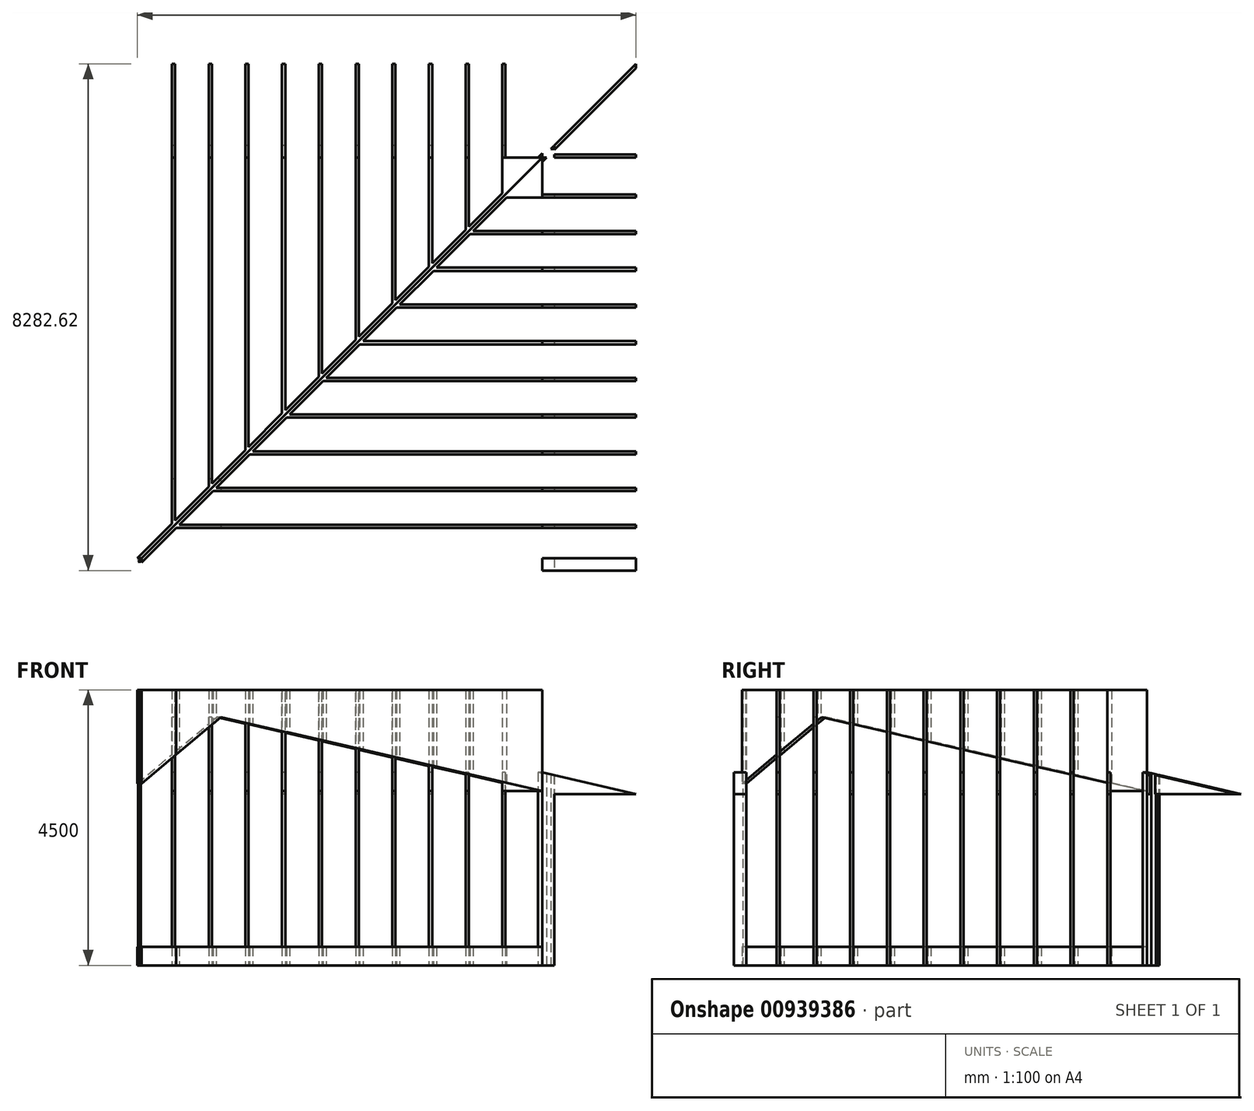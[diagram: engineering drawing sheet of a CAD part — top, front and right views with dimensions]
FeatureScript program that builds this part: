
annotation { "Feature Type Name" : "Feature", "Feature Type Description" : "" }
export const myFeature = defineFeature(function(context is Context, id is Id, definition is map)
    precondition{}
    {
        {
            var Q0;
            Q0=qCreatedBy(makeId("Top.planeOp"),FACE);
            var sketch = newSketch(context, id + "F0", { "sketchPlane" : qUnion([Q0])});
            skLineSegment(sketch, "E0.bottom", {"start": v(0, 0) * mm, "end": v(-6549, 0) * mm});
            skLineSegment(sketch, "E0.top", {"start": v(0, -6549) * mm, "end": v(-6549, -6549) * mm});
            skLineSegment(sketch, "E0.left", {"start": v(0, 0) * mm, "end": v(0, -6549) * mm});
            skLineSegment(sketch, "E0.right", {"start": v(-6549, 0) * mm, "end": v(-6549, -6549) * mm});
            skLineSegment(sketch, "E1.bottom", {"start": v(200, 200) * mm, "end": v(-6749, 200) * mm});
            skLineSegment(sketch, "E1.top", {"start": v(200, -6749) * mm, "end": v(-6749, -6749) * mm});
            skLineSegment(sketch, "E1.left", {"start": v(200, 200) * mm, "end": v(200, -6749) * mm});
            skLineSegment(sketch, "E1.right", {"start": v(-6749, 200) * mm, "end": v(-6749, -6749) * mm});
            skLineSegment(sketch, "E2.bottom", {"start": v(200, 200) * mm, "end": v(0, 200) * mm});
            skLineSegment(sketch, "E2.top", {"start": v(200, 0) * mm, "end": v(0, 0) * mm});
            skLineSegment(sketch, "E2.left", {"start": v(200, 200) * mm, "end": v(200, 0) * mm});
            skLineSegment(sketch, "E2.right", {"start": v(0, 200) * mm, "end": v(0, 0) * mm});
            skLineSegment(sketch, "E3.bottom", {"start": v(-6749, -6749) * mm, "end": v(-6549, -6749) * mm});
            skLineSegment(sketch, "E3.top", {"start": v(-6749, -6549) * mm, "end": v(-6549, -6549) * mm});
            skLineSegment(sketch, "E3.left", {"start": v(-6749, -6749) * mm, "end": v(-6749, -6549) * mm});
            skLineSegment(sketch, "E3.right", {"start": v(-6549, -6749) * mm, "end": v(-6549, -6549) * mm});
            skLineSegment(sketch, "E4", {"start": v(-6749, -6679) * mm, "end": v(130, 200) * mm});
            skLineSegment(sketch, "E5", {"start": v(200, 130) * mm, "end": v(-6679, -6749) * mm});
            skLineSegment(sketch, "E6", {"start": v(0, -600) * mm, "end": v(-530, -600) * mm});
            skLineSegment(sketch, "E7", {"start": v(0, -651) * mm, "end": v(-581, -651) * mm});
            skLineSegment(sketch, "E8", {"start": v(0, -1200) * mm, "end": v(-1130, -1200) * mm});
            skLineSegment(sketch, "E9", {"start": v(0, -1251) * mm, "end": v(-1181, -1251) * mm});
            skLineSegment(sketch, "E10", {"start": v(0, -1800) * mm, "end": v(-1730, -1800) * mm});
            skLineSegment(sketch, "E11", {"start": v(0, -1851) * mm, "end": v(-1781, -1851) * mm});
            skLineSegment(sketch, "E12", {"start": v(0, -2400) * mm, "end": v(-2330, -2400) * mm});
            skLineSegment(sketch, "E13", {"start": v(-2381, -2451) * mm, "end": v(0, -2451) * mm});
            skLineSegment(sketch, "E14", {"start": v(-2930, -3000) * mm, "end": v(0, -3000) * mm});
            skLineSegment(sketch, "E15", {"start": v(-3530, -3600) * mm, "end": v(0, -3600) * mm});
            skLineSegment(sketch, "E16", {"start": v(-2981, -3051) * mm, "end": v(0, -3051) * mm});
            skLineSegment(sketch, "E17", {"start": v(-3581, -3651) * mm, "end": v(0, -3651) * mm});
            skLineSegment(sketch, "E18", {"start": v(-4130, -4200) * mm, "end": v(0, -4200) * mm});
            skLineSegment(sketch, "E19", {"start": v(-4181, -4251) * mm, "end": v(0, -4251) * mm});
            skLineSegment(sketch, "E20", {"start": v(-4730, -4800) * mm, "end": v(0, -4800) * mm});
            skLineSegment(sketch, "E21", {"start": v(-4781, -4851) * mm, "end": v(0, -4851) * mm});
            skLineSegment(sketch, "E22", {"start": v(-5330, -5400) * mm, "end": v(0, -5400) * mm});
            skLineSegment(sketch, "E23", {"start": v(0, -5451) * mm, "end": v(-5381, -5451) * mm});
            skLineSegment(sketch, "E24", {"start": v(-5930, -6000) * mm, "end": v(0, -6000) * mm});
            skLineSegment(sketch, "E25", {"start": v(0, -6051) * mm, "end": v(-5981, -6051) * mm});
            skLineSegment(sketch, "E26", {"start": v(-6749, -6749) * mm, "end": v(200, 200) * mm});
            skLineSegment(sketch, "E27.bottom", {"start": v(0, -6000) * mm, "end": v(200, -6000) * mm});
            skLineSegment(sketch, "E27.top", {"start": v(0, -6051) * mm, "end": v(200, -6051) * mm});
            skLineSegment(sketch, "E27.left", {"start": v(0, -6000) * mm, "end": v(0, -6051) * mm});
            skLineSegment(sketch, "E27.right", {"start": v(200, -6000) * mm, "end": v(200, -6051) * mm});
            skLineSegment(sketch, "E28.bottom", {"start": v(0, -6549) * mm, "end": v(200, -6549) * mm});
            skLineSegment(sketch, "E28.top", {"start": v(0, -6749) * mm, "end": v(200, -6749) * mm});
            skLineSegment(sketch, "E28.left", {"start": v(0, -6549) * mm, "end": v(0, -6749) * mm});
            skLineSegment(sketch, "E28.right", {"start": v(200, -6549) * mm, "end": v(200, -6749) * mm});
            skLineSegment(sketch, "E29.bottom", {"start": v(0, -5400) * mm, "end": v(200, -5400) * mm});
            skLineSegment(sketch, "E29.top", {"start": v(0, -5451) * mm, "end": v(200, -5451) * mm});
            skLineSegment(sketch, "E29.left", {"start": v(0, -5400) * mm, "end": v(0, -5451) * mm});
            skLineSegment(sketch, "E29.right", {"start": v(200, -5400) * mm, "end": v(200, -5451) * mm});
            skLineSegment(sketch, "E30.bottom", {"start": v(0, -4800) * mm, "end": v(200, -4800) * mm});
            skLineSegment(sketch, "E30.top", {"start": v(0, -4851) * mm, "end": v(200, -4851) * mm});
            skLineSegment(sketch, "E30.left", {"start": v(0, -4800) * mm, "end": v(0, -4851) * mm});
            skLineSegment(sketch, "E30.right", {"start": v(200, -4800) * mm, "end": v(200, -4851) * mm});
            skLineSegment(sketch, "E31.bottom", {"start": v(0, -4200) * mm, "end": v(200, -4200) * mm});
            skLineSegment(sketch, "E31.top", {"start": v(0, -4251) * mm, "end": v(200, -4251) * mm});
            skLineSegment(sketch, "E31.left", {"start": v(0, -4200) * mm, "end": v(0, -4251) * mm});
            skLineSegment(sketch, "E31.right", {"start": v(200, -4200) * mm, "end": v(200, -4251) * mm});
            skLineSegment(sketch, "E32.bottom", {"start": v(0, -3600) * mm, "end": v(200, -3600) * mm});
            skLineSegment(sketch, "E32.top", {"start": v(0, -3651) * mm, "end": v(200, -3651) * mm});
            skLineSegment(sketch, "E32.left", {"start": v(0, -3600) * mm, "end": v(0, -3651) * mm});
            skLineSegment(sketch, "E32.right", {"start": v(200, -3600) * mm, "end": v(200, -3651) * mm});
            skLineSegment(sketch, "E33.bottom", {"start": v(0, -3000) * mm, "end": v(200, -3000) * mm});
            skLineSegment(sketch, "E33.top", {"start": v(0, -3051) * mm, "end": v(200, -3051) * mm});
            skLineSegment(sketch, "E33.left", {"start": v(0, -3000) * mm, "end": v(0, -3051) * mm});
            skLineSegment(sketch, "E33.right", {"start": v(200, -3000) * mm, "end": v(200, -3051) * mm});
            skLineSegment(sketch, "E34.bottom", {"start": v(0, -2400) * mm, "end": v(200, -2400) * mm});
            skLineSegment(sketch, "E34.top", {"start": v(0, -2451) * mm, "end": v(200, -2451) * mm});
            skLineSegment(sketch, "E34.left", {"start": v(0, -2400) * mm, "end": v(0, -2451) * mm});
            skLineSegment(sketch, "E34.right", {"start": v(200, -2400) * mm, "end": v(200, -2451) * mm});
            skLineSegment(sketch, "E35.bottom", {"start": v(0, -1800) * mm, "end": v(200, -1800) * mm});
            skLineSegment(sketch, "E35.top", {"start": v(0, -1851) * mm, "end": v(200, -1851) * mm});
            skLineSegment(sketch, "E35.left", {"start": v(0, -1800) * mm, "end": v(0, -1851) * mm});
            skLineSegment(sketch, "E35.right", {"start": v(200, -1800) * mm, "end": v(200, -1851) * mm});
            skLineSegment(sketch, "E36.bottom", {"start": v(0, -1200) * mm, "end": v(200, -1200) * mm});
            skLineSegment(sketch, "E36.top", {"start": v(0, -1251) * mm, "end": v(200, -1251) * mm});
            skLineSegment(sketch, "E36.left", {"start": v(0, -1200) * mm, "end": v(0, -1251) * mm});
            skLineSegment(sketch, "E36.right", {"start": v(200, -1200) * mm, "end": v(200, -1251) * mm});
            skLineSegment(sketch, "E37.bottom", {"start": v(0, -600) * mm, "end": v(200, -600) * mm});
            skLineSegment(sketch, "E37.top", {"start": v(0, -651) * mm, "end": v(200, -651) * mm});
            skLineSegment(sketch, "E37.left", {"start": v(0, -600) * mm, "end": v(0, -651) * mm});
            skLineSegment(sketch, "E37.right", {"start": v(200, -600) * mm, "end": v(200, -651) * mm});
            skLineSegment(sketch, "E38.bottom", {"start": v(188, 12) * mm, "end": v(12, 12) * mm});
            skLineSegment(sketch, "E38.top", {"start": v(188, 188) * mm, "end": v(12, 188) * mm});
            skLineSegment(sketch, "E38.left", {"start": v(188, 12) * mm, "end": v(188, 188) * mm});
            skLineSegment(sketch, "E38.right", {"start": v(12, 12) * mm, "end": v(12, 188) * mm});
            skLineSegment(sketch, "E39.bottom", {"start": v(188, 12) * mm, "end": v(143, 12) * mm});
            skLineSegment(sketch, "E39.top", {"start": v(188, 57) * mm, "end": v(143, 57) * mm});
            skLineSegment(sketch, "E39.left", {"start": v(188, 12) * mm, "end": v(188, 57) * mm});
            skLineSegment(sketch, "E39.right", {"start": v(143, 12) * mm, "end": v(143, 57) * mm});
            skLineSegment(sketch, "E40.bottom", {"start": v(12, 12) * mm, "end": v(57, 12) * mm});
            skLineSegment(sketch, "E40.top", {"start": v(12, 57) * mm, "end": v(57, 57) * mm});
            skLineSegment(sketch, "E40.left", {"start": v(12, 12) * mm, "end": v(12, 57) * mm});
            skLineSegment(sketch, "E40.right", {"start": v(57, 12) * mm, "end": v(57, 57) * mm});
            skLineSegment(sketch, "E41.bottom", {"start": v(188, 188) * mm, "end": v(143, 188) * mm});
            skLineSegment(sketch, "E41.top", {"start": v(188, 143) * mm, "end": v(143, 143) * mm});
            skLineSegment(sketch, "E41.left", {"start": v(188, 188) * mm, "end": v(188, 143) * mm});
            skLineSegment(sketch, "E41.right", {"start": v(143, 188) * mm, "end": v(143, 143) * mm});
            skLineSegment(sketch, "E42.bottom", {"start": v(12, 188) * mm, "end": v(57, 188) * mm});
            skLineSegment(sketch, "E42.top", {"start": v(12, 143) * mm, "end": v(57, 143) * mm});
            skLineSegment(sketch, "E42.left", {"start": v(12, 188) * mm, "end": v(12, 143) * mm});
            skLineSegment(sketch, "E42.right", {"start": v(57, 188) * mm, "end": v(57, 143) * mm});
            skLineSegment(sketch, "E43.bottom", {"start": v(200, -6749) * mm, "end": v(1700, -6749) * mm});
            skLineSegment(sketch, "E43.top", {"start": v(200, 200) * mm, "end": v(1700, 200) * mm});
            skLineSegment(sketch, "E43.left", {"start": v(200, -6749) * mm, "end": v(200, 200) * mm});
            skLineSegment(sketch, "E43.right", {"start": v(1700, -6749) * mm, "end": v(1700, 200) * mm});
            skLineSegment(sketch, "E44.bottom", {"start": v(200, -6549) * mm, "end": v(1700, -6549) * mm});
            skLineSegment(sketch, "E44.right", {"start": v(1700, -6549) * mm, "end": v(1700, -6749) * mm});
            skLineSegment(sketch, "E45.bottom", {"start": v(200, -6000) * mm, "end": v(1700, -6000) * mm});
            skLineSegment(sketch, "E45.top", {"start": v(200, -6051) * mm, "end": v(1700, -6051) * mm});
            skLineSegment(sketch, "E45.right", {"start": v(1700, -6000) * mm, "end": v(1700, -6051) * mm});
            skLineSegment(sketch, "E46.bottom", {"start": v(200, -5400) * mm, "end": v(1700, -5400) * mm});
            skLineSegment(sketch, "E46.top", {"start": v(200, -5451) * mm, "end": v(1700, -5451) * mm});
            skLineSegment(sketch, "E46.right", {"start": v(1700, -5400) * mm, "end": v(1700, -5451) * mm});
            skLineSegment(sketch, "E47.bottom", {"start": v(200, -4800) * mm, "end": v(1700, -4800) * mm});
            skLineSegment(sketch, "E47.top", {"start": v(200, -4851) * mm, "end": v(1700, -4851) * mm});
            skLineSegment(sketch, "E47.right", {"start": v(1700, -4800) * mm, "end": v(1700, -4851) * mm});
            skLineSegment(sketch, "E48.bottom", {"start": v(200, -4200) * mm, "end": v(1700, -4200) * mm});
            skLineSegment(sketch, "E48.top", {"start": v(200, -4251) * mm, "end": v(1700, -4251) * mm});
            skLineSegment(sketch, "E48.right", {"start": v(1700, -4200) * mm, "end": v(1700, -4251) * mm});
            skLineSegment(sketch, "E49.bottom", {"start": v(200, -3600) * mm, "end": v(1700, -3600) * mm});
            skLineSegment(sketch, "E49.top", {"start": v(200, -3651) * mm, "end": v(1700, -3651) * mm});
            skLineSegment(sketch, "E49.right", {"start": v(1700, -3600) * mm, "end": v(1700, -3651) * mm});
            skLineSegment(sketch, "E50.bottom", {"start": v(200, -3000) * mm, "end": v(1700, -3000) * mm});
            skLineSegment(sketch, "E50.top", {"start": v(200, -3051) * mm, "end": v(1700, -3051) * mm});
            skLineSegment(sketch, "E50.right", {"start": v(1700, -3000) * mm, "end": v(1700, -3051) * mm});
            skLineSegment(sketch, "E51.bottom", {"start": v(200, -2400) * mm, "end": v(1700, -2400) * mm});
            skLineSegment(sketch, "E51.top", {"start": v(200, -2451) * mm, "end": v(1700, -2451) * mm});
            skLineSegment(sketch, "E51.right", {"start": v(1700, -2400) * mm, "end": v(1700, -2451) * mm});
            skLineSegment(sketch, "E52.bottom", {"start": v(200, -1800) * mm, "end": v(1700, -1800) * mm});
            skLineSegment(sketch, "E52.top", {"start": v(200, -1851) * mm, "end": v(1700, -1851) * mm});
            skLineSegment(sketch, "E52.right", {"start": v(1700, -1800) * mm, "end": v(1700, -1851) * mm});
            skLineSegment(sketch, "E53.bottom", {"start": v(200, -1200) * mm, "end": v(1700, -1200) * mm});
            skLineSegment(sketch, "E53.top", {"start": v(200, -1251) * mm, "end": v(1700, -1251) * mm});
            skLineSegment(sketch, "E53.right", {"start": v(1700, -1200) * mm, "end": v(1700, -1251) * mm});
            skLineSegment(sketch, "E54.bottom", {"start": v(200, -600) * mm, "end": v(1700, -600) * mm});
            skLineSegment(sketch, "E54.top", {"start": v(200, -651) * mm, "end": v(1700, -651) * mm});
            skLineSegment(sketch, "E54.right", {"start": v(1700, -600) * mm, "end": v(1700, -651) * mm});
            skLineSegment(sketch, "E55.bottom", {"start": v(200, 0) * mm, "end": v(1700, 0) * mm});
            skLineSegment(sketch, "E55.top", {"start": v(200, 51) * mm, "end": v(1700, 51) * mm});
            skLineSegment(sketch, "E55.left", {"start": v(200, 0) * mm, "end": v(200, 51) * mm});
            skLineSegment(sketch, "E55.right", {"start": v(1700, 0) * mm, "end": v(1700, 51) * mm});
            skLineSegment(sketch, "E56.bottom", {"start": v(-6737, -6561) * mm, "end": v(-6561, -6561) * mm});
            skLineSegment(sketch, "E56.top", {"start": v(-6737, -6737) * mm, "end": v(-6561, -6737) * mm});
            skLineSegment(sketch, "E56.left", {"start": v(-6737, -6561) * mm, "end": v(-6737, -6737) * mm});
            skLineSegment(sketch, "E56.right", {"start": v(-6561, -6561) * mm, "end": v(-6561, -6737) * mm});
            skLineSegment(sketch, "E57.bottom", {"start": v(-6737, -6561) * mm, "end": v(-6692, -6561) * mm});
            skLineSegment(sketch, "E57.top", {"start": v(-6737, -6606) * mm, "end": v(-6692, -6606) * mm});
            skLineSegment(sketch, "E57.left", {"start": v(-6737, -6561) * mm, "end": v(-6737, -6606) * mm});
            skLineSegment(sketch, "E57.right", {"start": v(-6692, -6561) * mm, "end": v(-6692, -6606) * mm});
            skLineSegment(sketch, "E58.bottom", {"start": v(-6737, -6737) * mm, "end": v(-6692, -6737) * mm});
            skLineSegment(sketch, "E58.top", {"start": v(-6737, -6692) * mm, "end": v(-6692, -6692) * mm});
            skLineSegment(sketch, "E58.left", {"start": v(-6737, -6737) * mm, "end": v(-6737, -6692) * mm});
            skLineSegment(sketch, "E58.right", {"start": v(-6692, -6737) * mm, "end": v(-6692, -6692) * mm});
            skLineSegment(sketch, "E59.bottom", {"start": v(-6561, -6561) * mm, "end": v(-6606, -6561) * mm});
            skLineSegment(sketch, "E59.top", {"start": v(-6561, -6606) * mm, "end": v(-6606, -6606) * mm});
            skLineSegment(sketch, "E59.left", {"start": v(-6561, -6561) * mm, "end": v(-6561, -6606) * mm});
            skLineSegment(sketch, "E59.right", {"start": v(-6606, -6561) * mm, "end": v(-6606, -6606) * mm});
            skLineSegment(sketch, "E60.bottom", {"start": v(-6561, -6737) * mm, "end": v(-6606, -6737) * mm});
            skLineSegment(sketch, "E60.top", {"start": v(-6561, -6692) * mm, "end": v(-6606, -6692) * mm});
            skLineSegment(sketch, "E60.left", {"start": v(-6561, -6737) * mm, "end": v(-6561, -6692) * mm});
            skLineSegment(sketch, "E60.right", {"start": v(-6606, -6737) * mm, "end": v(-6606, -6692) * mm});
            skLineSegment(sketch, "E61", {"start": v(200, 130) * mm, "end": v(1700, 1630) * mm});
            skLineSegment(sketch, "E62", {"start": v(130, 200) * mm, "end": v(1700, 1770) * mm});
            skPoint(sketch, "E62.endSnap0", {"position": v(1700, 25.5) * mm});
            skLineSegment(sketch, "E63", {"start": v(1700, 1770) * mm, "end": v(1700, 1630) * mm});
            skLineSegment(sketch, "E64", {"start": v(200, 200) * mm, "end": v(1700, 1700) * mm});
            skSolve(sketch);
        }
        {
            var Q0;
            {var subQ1=sQuery(id+"F0.wireOp",EDGE,"E3.bottom");var subQ3=sQuery(id+"F0.wireOp",EDGE,"E5");var subQ4=makeQuery(id+"F0.imprint","INTERSECT",VERTEX,{"derivedFrom":[subQ1,subQ3]});Q0=makeQuery(id+"F0.imprint","IMPRINT",FACE,{"disambiguationData":[TD([[makeQuery(id+"F0.imprint","IMPRINT",EDGE,{"disambiguationData":[TD([[subQ4,1.0]])],"derivedFrom":subQ3}),1.0]])]});}
            var Q1;
            {var subQ3=sQuery(id+"F0.wireOp",EDGE,"E5");var subQ5=sQuery(id+"F0.wireOp",EDGE,"E2.left");var subQ7=makeQuery(id+"F0.imprint","INTERSECT",VERTEX,{"derivedFrom":[subQ5,subQ3]});Q1=makeQuery(id+"F0.imprint","IMPRINT",FACE,{"disambiguationData":[TD([[makeQuery(id+"F0.imprint","IMPRINT",EDGE,{"disambiguationData":[TD([[subQ7,-1.0]])],"derivedFrom":subQ3}),-1.0]])]});}
            var Q2;
            {var subQ1=sQuery(id+"F0.wireOp",EDGE,"E3.bottom");var subQ3=sQuery(id+"F0.wireOp",EDGE,"E5");var subQ4=makeQuery(id+"F0.imprint","INTERSECT",VERTEX,{"derivedFrom":[subQ1,subQ3]});Q2=makeQuery(id+"F0.imprint","IMPRINT",FACE,{"disambiguationData":[TD([[makeQuery(id+"F0.imprint","IMPRINT",EDGE,{"disambiguationData":[TD([[subQ4,1.0]])],"derivedFrom":subQ3}),-1.0]])]});}
            var Q3;
            {var subQ28=sQuery(id+"F0.wireOp",EDGE,"E1.top");Q3=makeQuery(id+"F0.imprint","IMPRINT",FACE,{"disambiguationData":[TD([[makeQuery(id+"F0.imprint","IMPRINT",EDGE,{"derivedFrom":subQ28}),-1.0]])]});}
            var Q4;
            {var subQ1=sQuery(id+"F0.wireOp",EDGE,"E0.top");var subQ3=sQuery(id+"F0.wireOp",EDGE,"E5");var subQ4=makeQuery(id+"F0.imprint","INTERSECT",VERTEX,{"derivedFrom":[subQ1,subQ3]});Q4=makeQuery(id+"F0.imprint","IMPRINT",FACE,{"disambiguationData":[TD([[makeQuery(id+"F0.imprint","IMPRINT",EDGE,{"disambiguationData":[TD([[subQ4,-1.0]])],"derivedFrom":subQ3}),-1.0]])]});}
            var Q5;
            {var subQ0=sQuery(id+"F0.wireOp",EDGE,"E5");var subQ13=makeQuery(id+"F0.imprint","INTERSECT",VERTEX,{"derivedFrom":[subQ0,sQuery(id+"F0.wireOp",EDGE,"E6")]});Q5=makeQuery(id+"F0.imprint","IMPRINT",FACE,{"disambiguationData":[TD([[makeQuery(id+"F0.imprint","IMPRINT",EDGE,{"disambiguationData":[TD([[subQ13,1.0]])],"derivedFrom":subQ0}),-1.0]])]});}
            var Q6;
            {var subQ0=sQuery(id+"F0.wireOp",EDGE,"E24");Q6=makeQuery(id+"F0.imprint","IMPRINT",FACE,{"disambiguationData":[TD([[makeQuery(id+"F0.imprint","IMPRINT",EDGE,{"derivedFrom":subQ0}),-1.0]])]});}
            var Q7;
            {var subQ0=sQuery(id+"F0.wireOp",EDGE,"E22");Q7=makeQuery(id+"F0.imprint","IMPRINT",FACE,{"disambiguationData":[TD([[makeQuery(id+"F0.imprint","IMPRINT",EDGE,{"derivedFrom":subQ0}),-1.0]])]});}
            var Q8;
            {var subQ0=sQuery(id+"F0.wireOp",EDGE,"E20");Q8=makeQuery(id+"F0.imprint","IMPRINT",FACE,{"disambiguationData":[TD([[makeQuery(id+"F0.imprint","IMPRINT",EDGE,{"derivedFrom":subQ0}),-1.0]])]});}
            var Q9;
            {var subQ0=sQuery(id+"F0.wireOp",EDGE,"E18");Q9=makeQuery(id+"F0.imprint","IMPRINT",FACE,{"disambiguationData":[TD([[makeQuery(id+"F0.imprint","IMPRINT",EDGE,{"derivedFrom":subQ0}),-1.0]])]});}
            var Q10;
            {var subQ0=sQuery(id+"F0.wireOp",EDGE,"E15");Q10=makeQuery(id+"F0.imprint","IMPRINT",FACE,{"disambiguationData":[TD([[makeQuery(id+"F0.imprint","IMPRINT",EDGE,{"derivedFrom":subQ0}),-1.0]])]});}
            var Q11;
            {var subQ0=sQuery(id+"F0.wireOp",EDGE,"E14");Q11=makeQuery(id+"F0.imprint","IMPRINT",FACE,{"disambiguationData":[TD([[makeQuery(id+"F0.imprint","IMPRINT",EDGE,{"derivedFrom":subQ0}),-1.0]])]});}
            var Q12;
            {var subQ0=sQuery(id+"F0.wireOp",EDGE,"E12");Q12=makeQuery(id+"F0.imprint","IMPRINT",FACE,{"disambiguationData":[TD([[makeQuery(id+"F0.imprint","IMPRINT",EDGE,{"derivedFrom":subQ0}),1.0]])]});}
            var Q13;
            {var subQ0=sQuery(id+"F0.wireOp",EDGE,"E10");Q13=makeQuery(id+"F0.imprint","IMPRINT",FACE,{"disambiguationData":[TD([[makeQuery(id+"F0.imprint","IMPRINT",EDGE,{"derivedFrom":subQ0}),1.0]])]});}
            var Q14;
            {var subQ0=sQuery(id+"F0.wireOp",EDGE,"E8");Q14=makeQuery(id+"F0.imprint","IMPRINT",FACE,{"disambiguationData":[TD([[makeQuery(id+"F0.imprint","IMPRINT",EDGE,{"derivedFrom":subQ0}),1.0]])]});}
            var Q15;
            {var subQ0=sQuery(id+"F0.wireOp",EDGE,"E6");Q15=makeQuery(id+"F0.imprint","IMPRINT",FACE,{"disambiguationData":[TD([[makeQuery(id+"F0.imprint","IMPRINT",EDGE,{"derivedFrom":subQ0}),1.0]])]});}
            var Q16;
            {var subQ1=sQuery(id+"F0.wireOp",EDGE,"E0.left");var subQ3=sQuery(id+"F0.wireOp",EDGE,"E5");var subQ4=makeQuery(id+"F0.imprint","INTERSECT",VERTEX,{"derivedFrom":[subQ1,subQ3]});Q16=makeQuery(id+"F0.imprint","IMPRINT",FACE,{"disambiguationData":[TD([[makeQuery(id+"F0.imprint","IMPRINT",EDGE,{"disambiguationData":[TD([[subQ4,1.0]])],"derivedFrom":subQ3}),-1.0]])]});}
            var Q17;
            Q17=makeQuery(id+"F0.imprint","IMPRINT",FACE,{"disambiguationData":[TD([[makeQuery(id+"F0.imprint","IMPRINT",EDGE,{"derivedFrom":sQuery(id+"F0.wireOp",EDGE,"E28.bottom")}),-1.0]])]});
            var Q18;
            Q18=makeQuery(id+"F0.imprint","IMPRINT",FACE,{"disambiguationData":[TD([[makeQuery(id+"F0.imprint","IMPRINT",EDGE,{"derivedFrom":sQuery(id+"F0.wireOp",EDGE,"E27.bottom")}),-1.0]])]});
            var Q19;
            Q19=makeQuery(id+"F0.imprint","IMPRINT",FACE,{"disambiguationData":[TD([[makeQuery(id+"F0.imprint","IMPRINT",EDGE,{"derivedFrom":sQuery(id+"F0.wireOp",EDGE,"E29.bottom")}),-1.0]])]});
            var Q20;
            Q20=makeQuery(id+"F0.imprint","IMPRINT",FACE,{"disambiguationData":[TD([[makeQuery(id+"F0.imprint","IMPRINT",EDGE,{"derivedFrom":sQuery(id+"F0.wireOp",EDGE,"E30.bottom")}),-1.0]])]});
            var Q21;
            Q21=makeQuery(id+"F0.imprint","IMPRINT",FACE,{"disambiguationData":[TD([[makeQuery(id+"F0.imprint","IMPRINT",EDGE,{"derivedFrom":sQuery(id+"F0.wireOp",EDGE,"E31.bottom")}),-1.0]])]});
            var Q22;
            Q22=makeQuery(id+"F0.imprint","IMPRINT",FACE,{"disambiguationData":[TD([[makeQuery(id+"F0.imprint","IMPRINT",EDGE,{"derivedFrom":sQuery(id+"F0.wireOp",EDGE,"E32.bottom")}),-1.0]])]});
            var Q23;
            Q23=makeQuery(id+"F0.imprint","IMPRINT",FACE,{"disambiguationData":[TD([[makeQuery(id+"F0.imprint","IMPRINT",EDGE,{"derivedFrom":sQuery(id+"F0.wireOp",EDGE,"E33.bottom")}),-1.0]])]});
            var Q24;
            Q24=makeQuery(id+"F0.imprint","IMPRINT",FACE,{"disambiguationData":[TD([[makeQuery(id+"F0.imprint","IMPRINT",EDGE,{"derivedFrom":sQuery(id+"F0.wireOp",EDGE,"E34.bottom")}),-1.0]])]});
            var Q25;
            Q25=makeQuery(id+"F0.imprint","IMPRINT",FACE,{"disambiguationData":[TD([[makeQuery(id+"F0.imprint","IMPRINT",EDGE,{"derivedFrom":sQuery(id+"F0.wireOp",EDGE,"E35.bottom")}),-1.0]])]});
            var Q26;
            Q26=makeQuery(id+"F0.imprint","IMPRINT",FACE,{"disambiguationData":[TD([[makeQuery(id+"F0.imprint","IMPRINT",EDGE,{"derivedFrom":sQuery(id+"F0.wireOp",EDGE,"E36.bottom")}),-1.0]])]});
            var Q27;
            Q27=makeQuery(id+"F0.imprint","IMPRINT",FACE,{"disambiguationData":[TD([[makeQuery(id+"F0.imprint","IMPRINT",EDGE,{"derivedFrom":sQuery(id+"F0.wireOp",EDGE,"E37.bottom")}),-1.0]])]});
            var Q28;
            {var subQ0=sQuery(id+"F0.wireOp",EDGE,"E40.bottom");Q28=makeQuery(id+"F0.imprint","IMPRINT",FACE,{"disambiguationData":[TD([[makeQuery(id+"F0.imprint","IMPRINT",EDGE,{"derivedFrom":subQ0}),-1.0]])]});}
            var Q29;
            {var subQ0=sQuery(id+"F0.wireOp",EDGE,"E40.bottom");Q29=makeQuery(id+"F0.imprint","IMPRINT",FACE,{"disambiguationData":[TD([[makeQuery(id+"F0.imprint","IMPRINT",EDGE,{"derivedFrom":subQ0}),1.0]])]});}
            var Q30;
            Q30=makeQuery(id+"F0.imprint","IMPRINT",FACE,{"disambiguationData":[TD([[makeQuery(id+"F0.imprint","IMPRINT",EDGE,{"derivedFrom":sQuery(id+"F0.wireOp",EDGE,"E39.bottom")}),-1.0]])]});
            var Q31;
            {var subQ2=sQuery(id+"F0.wireOp",EDGE,"E41.top");Q31=makeQuery(id+"F0.imprint","IMPRINT",FACE,{"disambiguationData":[TD([[makeQuery(id+"F0.imprint","IMPRINT",EDGE,{"derivedFrom":subQ2}),-1.0]])]});}
            var Q32;
            Q32=makeQuery(id+"F0.imprint","IMPRINT",FACE,{"disambiguationData":[TD([[makeQuery(id+"F0.imprint","IMPRINT",EDGE,{"derivedFrom":sQuery(id+"F0.wireOp",EDGE,"E44.bottom")}),-1.0]])]});
            var Q33;
            Q33=makeQuery(id+"F0.imprint","IMPRINT",FACE,{"disambiguationData":[TD([[makeQuery(id+"F0.imprint","IMPRINT",EDGE,{"derivedFrom":sQuery(id+"F0.wireOp",EDGE,"E45.bottom")}),-1.0]])]});
            var Q34;
            Q34=makeQuery(id+"F0.imprint","IMPRINT",FACE,{"disambiguationData":[TD([[makeQuery(id+"F0.imprint","IMPRINT",EDGE,{"derivedFrom":sQuery(id+"F0.wireOp",EDGE,"E46.bottom")}),-1.0]])]});
            var Q35;
            Q35=makeQuery(id+"F0.imprint","IMPRINT",FACE,{"disambiguationData":[TD([[makeQuery(id+"F0.imprint","IMPRINT",EDGE,{"derivedFrom":sQuery(id+"F0.wireOp",EDGE,"E47.bottom")}),-1.0]])]});
            var Q36;
            Q36=makeQuery(id+"F0.imprint","IMPRINT",FACE,{"disambiguationData":[TD([[makeQuery(id+"F0.imprint","IMPRINT",EDGE,{"derivedFrom":sQuery(id+"F0.wireOp",EDGE,"E48.bottom")}),-1.0]])]});
            var Q37;
            Q37=makeQuery(id+"F0.imprint","IMPRINT",FACE,{"disambiguationData":[TD([[makeQuery(id+"F0.imprint","IMPRINT",EDGE,{"derivedFrom":sQuery(id+"F0.wireOp",EDGE,"E49.bottom")}),-1.0]])]});
            var Q38;
            Q38=makeQuery(id+"F0.imprint","IMPRINT",FACE,{"disambiguationData":[TD([[makeQuery(id+"F0.imprint","IMPRINT",EDGE,{"derivedFrom":sQuery(id+"F0.wireOp",EDGE,"E50.bottom")}),-1.0]])]});
            var Q39;
            Q39=makeQuery(id+"F0.imprint","IMPRINT",FACE,{"disambiguationData":[TD([[makeQuery(id+"F0.imprint","IMPRINT",EDGE,{"derivedFrom":sQuery(id+"F0.wireOp",EDGE,"E51.bottom")}),-1.0]])]});
            var Q40;
            Q40=makeQuery(id+"F0.imprint","IMPRINT",FACE,{"disambiguationData":[TD([[makeQuery(id+"F0.imprint","IMPRINT",EDGE,{"derivedFrom":sQuery(id+"F0.wireOp",EDGE,"E52.bottom")}),-1.0]])]});
            var Q41;
            Q41=makeQuery(id+"F0.imprint","IMPRINT",FACE,{"disambiguationData":[TD([[makeQuery(id+"F0.imprint","IMPRINT",EDGE,{"derivedFrom":sQuery(id+"F0.wireOp",EDGE,"E53.bottom")}),-1.0]])]});
            var Q42;
            Q42=makeQuery(id+"F0.imprint","IMPRINT",FACE,{"disambiguationData":[TD([[makeQuery(id+"F0.imprint","IMPRINT",EDGE,{"derivedFrom":sQuery(id+"F0.wireOp",EDGE,"E54.bottom")}),-1.0]])]});
            var Q43;
            Q43=makeQuery(id+"F0.imprint","IMPRINT",FACE,{"disambiguationData":[TD([[makeQuery(id+"F0.imprint","IMPRINT",EDGE,{"derivedFrom":sQuery(id+"F0.wireOp",EDGE,"E55.bottom")}),1.0]])]});
            var Q44;
            {var subQ1=sQuery(id+"F0.wireOp",EDGE,"E3.bottom");var subQ3=sQuery(id+"F0.wireOp",EDGE,"E5");var subQ4=makeQuery(id+"F0.imprint","INTERSECT",VERTEX,{"derivedFrom":[subQ1,subQ3]});Q44=makeQuery(id+"F0.imprint","IMPRINT",FACE,{"disambiguationData":[TD([[makeQuery(id+"F0.imprint","IMPRINT",EDGE,{"disambiguationData":[TD([[subQ4,1.0]])],"derivedFrom":subQ3}),1.0]])]});}
            var Q45;
            {var subQ0=sQuery(id+"F0.wireOp",EDGE,"E39.bottom");Q45=makeQuery(id+"F0.imprint","IMPRINT",FACE,{"disambiguationData":[TD([[makeQuery(id+"F0.imprint","IMPRINT",EDGE,{"derivedFrom":subQ0}),1.0]])]});}
            var Q46;
            {var subQ0=sQuery(id+"F0.wireOp",EDGE,"E41.left");Q46=makeQuery(id+"F0.imprint","IMPRINT",FACE,{"disambiguationData":[TD([[makeQuery(id+"F0.imprint","IMPRINT",EDGE,{"derivedFrom":subQ0}),1.0]])]});}
            var Q47;
            {var subQ0=sQuery(id+"F0.wireOp",EDGE,"E58.bottom");Q47=makeQuery(id+"F0.imprint","IMPRINT",FACE,{"disambiguationData":[TD([[makeQuery(id+"F0.imprint","IMPRINT",EDGE,{"derivedFrom":subQ0}),1.0]])]});}
            var Q48;
            Q48=makeQuery(id+"F0.imprint","IMPRINT",FACE,{"disambiguationData":[TD([[makeQuery(id+"F0.imprint","IMPRINT",EDGE,{"derivedFrom":sQuery(id+"F0.wireOp",EDGE,"E60.bottom")}),-1.0]])]});
            var Q49;
            {var subQ2=sQuery(id+"F0.wireOp",EDGE,"E59.top");Q49=makeQuery(id+"F0.imprint","IMPRINT",FACE,{"disambiguationData":[TD([[makeQuery(id+"F0.imprint","IMPRINT",EDGE,{"derivedFrom":subQ2}),-1.0]])]});}
            var Q50;
            {var subQ0=sQuery(id+"F0.wireOp",EDGE,"E59.left");Q50=makeQuery(id+"F0.imprint","IMPRINT",FACE,{"disambiguationData":[TD([[makeQuery(id+"F0.imprint","IMPRINT",EDGE,{"derivedFrom":subQ0}),1.0]])]});}
            var Q51;
            {var subQ0=sQuery(id+"F0.wireOp",EDGE,"E64");Q51=makeQuery(id+"F0.imprint","IMPRINT",FACE,{"disambiguationData":[TD([[makeQuery(id+"F0.imprint","IMPRINT",EDGE,{"derivedFrom":subQ0}),-1.0]])]});}
            var Q52;
            {var subQ1=sQuery(id+"F0.wireOp",EDGE,"E43.top");var subQ3=sQuery(id+"F0.wireOp",EDGE,"E61");var subQ4=makeQuery(id+"F0.imprint","INTERSECT",VERTEX,{"derivedFrom":[subQ1,subQ3]});Q52=makeQuery(id+"F0.imprint","IMPRINT",FACE,{"disambiguationData":[TD([[makeQuery(id+"F0.imprint","IMPRINT",EDGE,{"disambiguationData":[TD([[subQ4,1.0]])],"derivedFrom":subQ3}),1.0]])]});}
            extrude(context, id + "F1", {"entities" : qUnion([Q0, Q1, Q2, Q3, Q4, Q5, Q6, Q7, Q8, Q9, Q10, Q11, Q12, Q13, Q14, Q15, Q16, Q17, Q18, Q19, Q20, Q21, Q22, Q23, Q24, Q25, Q26, Q27, Q28, Q29, Q30, Q31, Q32, Q33, Q34, Q35, Q36, Q37, Q38, Q39, Q40, Q41, Q42, Q43, Q44, Q45, Q46, Q47, Q48, Q49, Q50, Q51, Q52]), "depth" : 4500 * mm, "offsetDistance" : 25 * mm});
        }
        {
            var Q0;
            Q0=makeQuery(id+"F1.opExtrude","SWEPT_FACE",FACE,{"disambiguationData":[OSD([sQuery(id+"F0.wireOp",EDGE,"E1.top"),sQuery(id+"F0.wireOp",EDGE,"E3.bottom"),sQuery(id+"F0.wireOp",EDGE,"E28.top"),sQuery(id+"F0.wireOp",EDGE,"E43.bottom")])]});
            var sketch = newSketch(context, id + "F2", { "sketchPlane" : qUnion([Q0])});
            skLineSegment(sketch, "E65", {"start": v(-6749, 0) * mm, "end": v(-6749, 2800) * mm});
            skLineSegment(sketch, "E66", {"start": v(-6749, 2800) * mm, "end": v(-7215.72, 2800) * mm});
            skLineSegment(sketch, "E67", {"start": v(-7215.72, 2800) * mm, "end": v(-5327.86, 4384.1) * mm});
            skLineSegment(sketch, "E68", {"start": v(-5327.86, 4384.1) * mm, "end": v(1533.62, 2800) * mm});
            skLineSegment(sketch, "E69", {"start": v(1533.62, 2800) * mm, "end": v(200, 2800) * mm});
            skLineSegment(sketch, "E70", {"start": v(200, 2800) * mm, "end": v(200, 0) * mm});
            skLineSegment(sketch, "E71", {"start": v(200, 0) * mm, "end": v(-6749, 0) * mm});
            skLineSegment(sketch, "E72", {"start": v(-6549, 300) * mm, "end": v(-6549, 2967.82) * mm});
            skLineSegment(sketch, "E73", {"start": v(-6549, 2967.82) * mm, "end": v(-5249.6, 4058.14) * mm});
            skLineSegment(sketch, "E74", {"start": v(-5249.6, 4058.14) * mm, "end": v(0, 2846.17) * mm});
            skLineSegment(sketch, "E75", {"start": v(0, 2846.17) * mm, "end": v(0, 300) * mm});
            skLineSegment(sketch, "E76", {"start": v(0, 300) * mm, "end": v(-6549, 300) * mm});
            skLineSegment(sketch, "E77", {"start": v(0, 2846.17) * mm, "end": v(200, 2800) * mm});
            skLineSegment(sketch, "E78", {"start": v(-6549, 2967.82) * mm, "end": v(-6749, 2800) * mm});
            skSolve(sketch);
        }
        {
            var Q0;
            Q0=makeQuery(id+"F2.imprint","IMPRINT",FACE,{"disambiguationData":[TD([[makeQuery(id+"F2.imprint","IMPRINT",EDGE,{"derivedFrom":sQuery(id+"F2.wireOp",EDGE,"E72")}),-1.0]])]});
            var Q1;
            {var subQ8=sQuery(id+"F2.wireOp",EDGE,"E68");Q1=makeQuery(id+"F2.imprint","IMPRINT",FACE,{"disambiguationData":[TD([[makeQuery(id+"F2.imprint","IMPRINT",EDGE,{"derivedFrom":subQ8}),1.0]])]});}
            extrude(context, id + "F3", {"entities" : qUnion([Q0, Q1]), "operationType" : NewBodyOperationType.REMOVE, "endBound" : BoundingType.THROUGH_ALL, "oppositeDirection" : true, "depth" : 25 * mm, "offsetDistance" : 25 * mm});
        }
        {
            var Q0;
            Q0=makeQuery(id+"F1.opExtrude","SWEPT_BODY",BODY,{"disambiguationData":[OSD([sQuery(id+"F0.wireOp",EDGE,"E0.top"),sQuery(id+"F0.wireOp",EDGE,"E1.top"),sQuery(id+"F0.wireOp",EDGE,"E2.top"),sQuery(id+"F0.wireOp",EDGE,"E3.bottom"),sQuery(id+"F0.wireOp",EDGE,"E5"),sQuery(id+"F0.wireOp",EDGE,"E6"),sQuery(id+"F0.wireOp",EDGE,"E7"),sQuery(id+"F0.wireOp",EDGE,"E8"),sQuery(id+"F0.wireOp",EDGE,"E9"),sQuery(id+"F0.wireOp",EDGE,"E10"),sQuery(id+"F0.wireOp",EDGE,"E11"),sQuery(id+"F0.wireOp",EDGE,"E12"),sQuery(id+"F0.wireOp",EDGE,"E13"),sQuery(id+"F0.wireOp",EDGE,"E14"),sQuery(id+"F0.wireOp",EDGE,"E15"),sQuery(id+"F0.wireOp",EDGE,"E16"),sQuery(id+"F0.wireOp",EDGE,"E17"),sQuery(id+"F0.wireOp",EDGE,"E18"),sQuery(id+"F0.wireOp",EDGE,"E19"),sQuery(id+"F0.wireOp",EDGE,"E20"),sQuery(id+"F0.wireOp",EDGE,"E21"),sQuery(id+"F0.wireOp",EDGE,"E22"),sQuery(id+"F0.wireOp",EDGE,"E23"),sQuery(id+"F0.wireOp",EDGE,"E24"),sQuery(id+"F0.wireOp",EDGE,"E25"),sQuery(id+"F0.wireOp",EDGE,"E26"),sQuery(id+"F0.wireOp",EDGE,"E27.bottom"),sQuery(id+"F0.wireOp",EDGE,"E27.top"),sQuery(id+"F0.wireOp",EDGE,"E28.bottom"),sQuery(id+"F0.wireOp",EDGE,"E28.top"),sQuery(id+"F0.wireOp",EDGE,"E29.bottom"),sQuery(id+"F0.wireOp",EDGE,"E29.top"),sQuery(id+"F0.wireOp",EDGE,"E30.bottom"),sQuery(id+"F0.wireOp",EDGE,"E30.top"),sQuery(id+"F0.wireOp",EDGE,"E31.bottom"),sQuery(id+"F0.wireOp",EDGE,"E31.top"),sQuery(id+"F0.wireOp",EDGE,"E32.bottom"),sQuery(id+"F0.wireOp",EDGE,"E32.top"),sQuery(id+"F0.wireOp",EDGE,"E33.bottom"),sQuery(id+"F0.wireOp",EDGE,"E33.top"),sQuery(id+"F0.wireOp",EDGE,"E34.bottom"),sQuery(id+"F0.wireOp",EDGE,"E34.top"),sQuery(id+"F0.wireOp",EDGE,"E35.bottom"),sQuery(id+"F0.wireOp",EDGE,"E35.top"),sQuery(id+"F0.wireOp",EDGE,"E36.bottom"),sQuery(id+"F0.wireOp",EDGE,"E36.top"),sQuery(id+"F0.wireOp",EDGE,"E37.bottom"),sQuery(id+"F0.wireOp",EDGE,"E37.top"),sQuery(id+"F0.wireOp",EDGE,"E38.bottom"),sQuery(id+"F0.wireOp",EDGE,"E38.left"),sQuery(id+"F0.wireOp",EDGE,"E39.top"),sQuery(id+"F0.wireOp",EDGE,"E39.right"),sQuery(id+"F0.wireOp",EDGE,"E40.right"),sQuery(id+"F0.wireOp",EDGE,"E41.top"),sQuery(id+"F0.wireOp",EDGE,"E43.left"),sQuery(id+"F0.wireOp",EDGE,"E44.bottom"),sQuery(id+"F0.wireOp",EDGE,"E43.bottom"),sQuery(id+"F0.wireOp",EDGE,"E44.right"),sQuery(id+"F0.wireOp",EDGE,"E45.bottom"),sQuery(id+"F0.wireOp",EDGE,"E45.top"),sQuery(id+"F0.wireOp",EDGE,"E45.right"),sQuery(id+"F0.wireOp",EDGE,"E46.bottom"),sQuery(id+"F0.wireOp",EDGE,"E46.top"),sQuery(id+"F0.wireOp",EDGE,"E46.right"),sQuery(id+"F0.wireOp",EDGE,"E47.bottom"),sQuery(id+"F0.wireOp",EDGE,"E47.top"),sQuery(id+"F0.wireOp",EDGE,"E47.right"),sQuery(id+"F0.wireOp",EDGE,"E48.bottom"),sQuery(id+"F0.wireOp",EDGE,"E48.top"),sQuery(id+"F0.wireOp",EDGE,"E48.right"),sQuery(id+"F0.wireOp",EDGE,"E49.bottom"),sQuery(id+"F0.wireOp",EDGE,"E49.top"),sQuery(id+"F0.wireOp",EDGE,"E49.right"),sQuery(id+"F0.wireOp",EDGE,"E50.bottom"),sQuery(id+"F0.wireOp",EDGE,"E50.top"),sQuery(id+"F0.wireOp",EDGE,"E50.right"),sQuery(id+"F0.wireOp",EDGE,"E51.bottom"),sQuery(id+"F0.wireOp",EDGE,"E51.top"),sQuery(id+"F0.wireOp",EDGE,"E51.right"),sQuery(id+"F0.wireOp",EDGE,"E52.bottom"),sQuery(id+"F0.wireOp",EDGE,"E52.top"),sQuery(id+"F0.wireOp",EDGE,"E52.right"),sQuery(id+"F0.wireOp",EDGE,"E53.bottom"),sQuery(id+"F0.wireOp",EDGE,"E53.top"),sQuery(id+"F0.wireOp",EDGE,"E53.right"),sQuery(id+"F0.wireOp",EDGE,"E54.bottom"),sQuery(id+"F0.wireOp",EDGE,"E54.top"),sQuery(id+"F0.wireOp",EDGE,"E54.right"),sQuery(id+"F0.wireOp",EDGE,"E55.bottom"),sQuery(id+"F0.wireOp",EDGE,"E55.top"),sQuery(id+"F0.wireOp",EDGE,"E55.right")])]});
            var Q1;
            {var subQ0=sQuery(id+"F0.wireOp",EDGE,"E26");var subQ1=makeQuery(id+"F0.imprint","INTERSECT",VERTEX,{"derivedFrom":[subQ0,sQuery(id+"F0.wireOp",EDGE,"E40.bottom"),sQuery(id+"F0.wireOp",EDGE,"E40.left")]});var subQ2=makeQuery(id+"F0.imprint","INTERSECT",VERTEX,{"derivedFrom":[sQuery(id+"F0.wireOp",EDGE,"E0.bottom"),sQuery(id+"F0.wireOp",EDGE,"E0.left"),sQuery(id+"F0.wireOp",EDGE,"E2.top"),sQuery(id+"F0.wireOp",EDGE,"E2.right"),subQ0]});Q1=makeQuery(id+"F1.opExtrude","SWEPT_FACE",FACE,{"disambiguationData":[OSD([subQ0]),TDD([makeQuery(id+"F0.imprint","IMPRINT",EDGE,{"disambiguationData":[TD([[makeQuery(id+"F0.imprint","INTERSECT",VERTEX,{"derivedFrom":[sQuery(id+"F0.wireOp",EDGE,"E3.bottom"),sQuery(id+"F0.wireOp",EDGE,"E3.left"),subQ0]}),-1.0]])],"derivedFrom":subQ0}),makeQuery(id+"F0.imprint","IMPRINT",EDGE,{"disambiguationData":[TD([[subQ2,1.0]])],"derivedFrom":subQ0}),makeQuery(id+"F0.imprint","IMPRINT",EDGE,{"disambiguationData":[TD([[subQ1,1.0]])],"derivedFrom":subQ0}),makeQuery(id+"F0.imprint","IMPRINT",EDGE,{"disambiguationData":[TD([[subQ1,-1.0]])],"derivedFrom":subQ0})])]});}
            mirror(context, id + "F4", {"operationType" : NewBodyOperationType.ADD, "entities" : qUnion([Q0]), "mirrorPlane" : qUnion([Q1])});
        }
    });
